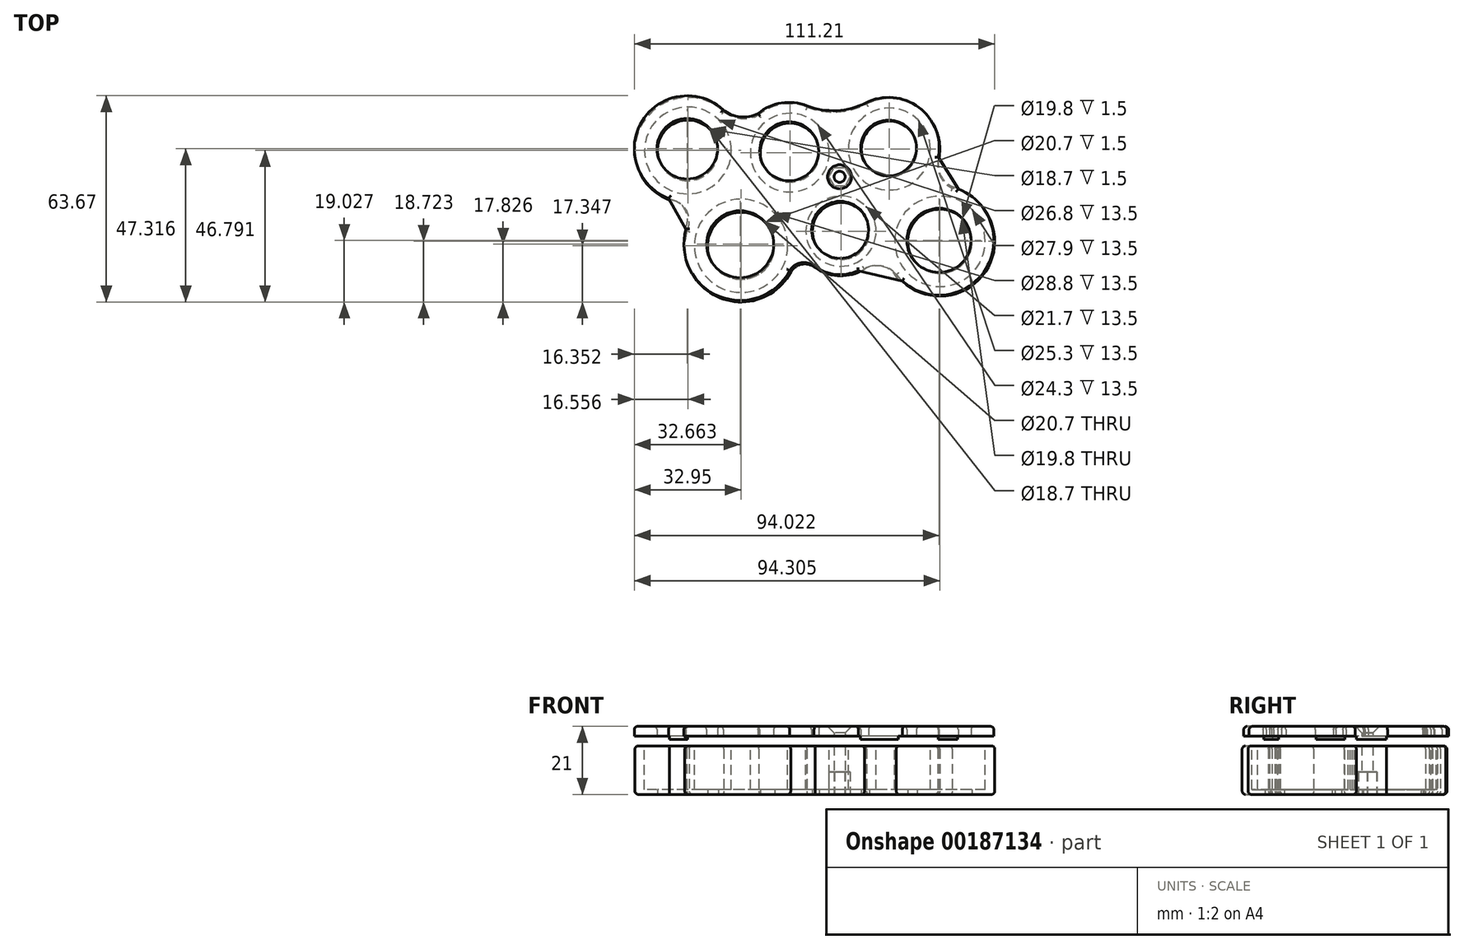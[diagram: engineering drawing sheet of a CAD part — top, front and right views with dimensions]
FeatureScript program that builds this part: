
annotation { "Feature Type Name" : "Feature", "Feature Type Description" : "" }
export const myFeature = defineFeature(function(context is Context, id is Id, definition is map)
    precondition{}
    {
        {
            var Q0;
            Q0=qCreatedBy(makeId("Top.planeOp"),FACE);
            var sketch = newSketch(context, id + "F0", { "sketchPlane" : qUnion([Q0])});
            skArc(sketch, "E0", {"start": v(-18.22, 23.12) * mm, "mid": v(-43.25, 19.71) * mm, "end": v(-35.08, -4.19) * mm});
            skArc(sketch, "E1", {"start": v(7.41, 24.56) * mm, "mid": v(-0.37, 25.32) * mm, "end": v(-7.48, 22.09) * mm});
            skArc(sketch, "E2", {"start": v(48.15, 8.81) * mm, "mid": v(42.1, 24.06) * mm, "end": v(25.77, 25.48) * mm});
            skArc(sketch, "E3", {"start": v(9.86, -25.02) * mm, "mid": v(17.41, -27.58) * mm, "end": v(25.12, -25.54) * mm});
            skArc(sketch, "E4", {"start": v(34.96, -27.17) * mm, "mid": v(62.62, -26.1) * mm, "end": v(52.17, -0.47) * mm});
            skArc(sketch, "E5", {"start": v(-29.65, -13.66) * mm, "mid": v(-19.4, -34.43) * mm, "end": v(2.37, -26.49) * mm});
            skArc(sketch, "E6", {"start": v(-29.65, -13.66) * mm, "mid": v(-29.77, -7.44) * mm, "end": v(-35.08, -4.19) * mm});
            skArc(sketch, "E7", {"start": v(-18.22, 23.12) * mm, "mid": v(-13.01, 20.97) * mm, "end": v(-7.48, 22.09) * mm});
            skArc(sketch, "E8", {"start": v(48.15, 8.81) * mm, "mid": v(48.38, 3.4) * mm, "end": v(52.17, -0.47) * mm});
            skArc(sketch, "E9", {"start": v(34.96, -27.17) * mm, "mid": v(30.34, -24.58) * mm, "end": v(25.12, -25.54) * mm});
            skArc(sketch, "E10", {"start": v(9.86, -25.02) * mm, "mid": v(5.77, -24) * mm, "end": v(2.37, -26.49) * mm});
            skCircle(sketch, "E11", {"center": v(-29.33, 11.12) * mm, "radius": 9.35 * mm});
            skCircle(sketch, "E12", {"center": v(-12.94, -18.32) * mm, "radius": 10.35 * mm});
            skCircle(sketch, "E13", {"center": v(2.1, 10.43) * mm, "radius": 9.1 * mm});
            skCircle(sketch, "E14", {"center": v(17.88, -13.8) * mm, "radius": 8.8 * mm});
            skCircle(sketch, "E15", {"center": v(32.79, 11.55) * mm, "radius": 8.6 * mm});
            skCircle(sketch, "E16", {"center": v(48.42, -16.95) * mm, "radius": 9.9 * mm});
            skPoint(sketch, "E17", {"position": v(17.46, 2.98) * mm});
            skPoint(sketch, "E18.orphan", {"position": v(17.45, 10.99) * mm});
            skPoint(sketch, "E19.orphan", {"position": v(25.33, -1.12) * mm});
            skPoint(sketch, "E20.trimOffspring.end.orphan", {"position": v(10, -1.68) * mm});
            skCircle(sketch, "E21", {"center": v(17.46, 2.98) * mm, "radius": 1.7 * mm});
            skPoint(sketch, "E22.center.orphan", {"position": v(16.6, 25.02) * mm});
            skArc(sketch, "E23", {"start": v(7.41, 24.56) * mm, "mid": v(16.7, 23.01) * mm, "end": v(25.77, 25.48) * mm});
            skSolve(sketch);
        }
        {
            var Q0;
            Q0=makeQuery(id+"F0.imprint","IMPRINT",FACE,{"disambiguationData":[TD([[makeQuery(id+"F0.imprint","IMPRINT",EDGE,{"derivedFrom":sQuery(id+"F0.wireOp",EDGE,"E0")}),1.0]])]});
            extrude(context, id + "F1", {"entities" : qUnion([Q0]), "depth" : 15 * mm});
        }
        {
            var Q0;
            Q0=qCreatedBy(makeId("Top.planeOp"),FACE);
            cPlane(context, id + "F2", {"entities" : qUnion([Q0]), "cplaneType" : CPlaneType.OFFSET, "offset" : 18 * mm, "width" : 150 * mm, "height" : 150 * mm});
        }
        {
            var Q0;
            Q0=makeQuery(id+"F1.opExtrude","CAP_FACE",FACE,{"disambiguationData":[OSD([sQuery(id+"F0.wireOp",EDGE,"E0"),sQuery(id+"F0.wireOp",EDGE,"E1"),sQuery(id+"F0.wireOp",EDGE,"E2"),sQuery(id+"F0.wireOp",EDGE,"E3"),sQuery(id+"F0.wireOp",EDGE,"E4"),sQuery(id+"F0.wireOp",EDGE,"E5"),sQuery(id+"F0.wireOp",EDGE,"E6"),sQuery(id+"F0.wireOp",EDGE,"E7"),sQuery(id+"F0.wireOp",EDGE,"E8"),sQuery(id+"F0.wireOp",EDGE,"E9"),sQuery(id+"F0.wireOp",EDGE,"E10"),sQuery(id+"F0.wireOp",EDGE,"cmuSQvfR-1LlV-bjM8-RssA-lsbDypLqzE8I"),sQuery(id+"F0.wireOp",EDGE,"E22"),sQuery(id+"F0.wireOp",EDGE,"E11"),sQuery(id+"F0.wireOp",EDGE,"E12"),sQuery(id+"F0.wireOp",EDGE,"E13"),sQuery(id+"F0.wireOp",EDGE,"E14"),sQuery(id+"F0.wireOp",EDGE,"E15"),sQuery(id+"F0.wireOp",EDGE,"E16")])],"isStart":false});
            var sketch = newSketch(context, id + "F3", { "sketchPlane" : qUnion([Q0])});
            skCircle(sketch, "E24", {"center": v(-29.33, 11.12) * mm, "radius": 13.4 * mm});
            skCircle(sketch, "E25", {"center": v(-12.94, -18.32) * mm, "radius": 14.4 * mm});
            skCircle(sketch, "E26", {"center": v(17.88, -13.8) * mm, "radius": 10.85 * mm});
            skCircle(sketch, "E27", {"center": v(2.1, 10.43) * mm, "radius": 12.15 * mm});
            skCircle(sketch, "E28", {"center": v(32.79, 11.55) * mm, "radius": 12.65 * mm});
            skCircle(sketch, "E29", {"center": v(48.42, -16.95) * mm, "radius": 13.95 * mm});
            skSolve(sketch);
        }
        {
            var Q0;
            Q0=makeQuery(id+"F3.imprint","IMPRINT",FACE,{"disambiguationData":[TD([[makeQuery(id+"F3.imprint","IMPRINT",EDGE,{"derivedFrom":sQuery(id+"F3.wireOp",EDGE,"E24")}),1.0]])]});
            var Q1;
            Q1=makeQuery(id+"F3.imprint","IMPRINT",FACE,{"disambiguationData":[TD([[makeQuery(id+"F3.imprint","IMPRINT",EDGE,{"derivedFrom":sQuery(id+"F3.wireOp",EDGE,"E27")}),1.0]])]});
            var Q2;
            Q2=makeQuery(id+"F3.imprint","IMPRINT",FACE,{"disambiguationData":[TD([[makeQuery(id+"F3.imprint","IMPRINT",EDGE,{"derivedFrom":sQuery(id+"F3.wireOp",EDGE,"E28")}),1.0]])]});
            var Q3;
            Q3=makeQuery(id+"F3.imprint","IMPRINT",FACE,{"disambiguationData":[TD([[makeQuery(id+"F3.imprint","IMPRINT",EDGE,{"derivedFrom":sQuery(id+"F3.wireOp",EDGE,"E26")}),1.0]])]});
            var Q4;
            Q4=makeQuery(id+"F3.imprint","IMPRINT",FACE,{"disambiguationData":[TD([[makeQuery(id+"F3.imprint","IMPRINT",EDGE,{"derivedFrom":sQuery(id+"F3.wireOp",EDGE,"E25")}),1.0]])]});
            var Q5;
            Q5=makeQuery(id+"F3.imprint","IMPRINT",FACE,{"disambiguationData":[TD([[makeQuery(id+"F3.imprint","IMPRINT",EDGE,{"derivedFrom":sQuery(id+"F3.wireOp",EDGE,"E29")}),1.0]])]});
            extrude(context, id + "F4", {"entities" : qUnion([Q0, Q1, Q2, Q3, Q4, Q5]), "operationType" : NewBodyOperationType.REMOVE, "oppositeDirection" : true, "depth" : 13.5 * mm});
        }
        {
            var Q0;
            Q0=qCreatedBy(makeId("Top.planeOp"),FACE);
            var sketch = newSketch(context, id + "F5", { "sketchPlane" : qUnion([Q0])});
            skPoint(sketch, "E30", {"position": v(17.46, 2.98) * mm});
            skCircle(sketch, "E31.cCircle", {"center": v(17.46, 2.98) * mm, "radius": 2.86 * mm, "construction": true});
            skLineSegment(sketch, "E31.0", {"start": v(19.06, 5.87) * mm, "end": v(20.76, 3.03) * mm});
            skLineSegment(sketch, "E31.1", {"start": v(20.76, 3.03) * mm, "end": v(19.15, 0.15) * mm});
            skLineSegment(sketch, "E31.2", {"start": v(19.15, 0.15) * mm, "end": v(15.85, 0.1) * mm});
            skLineSegment(sketch, "E31.3", {"start": v(15.85, 0.1) * mm, "end": v(14.16, 2.93) * mm});
            skLineSegment(sketch, "E31.4", {"start": v(14.16, 2.93) * mm, "end": v(15.76, 5.81) * mm});
            skLineSegment(sketch, "E31.5", {"start": v(15.76, 5.81) * mm, "end": v(19.06, 5.87) * mm});
            skPoint(sketch, "E31.0.midPoint", {"position": v(19.9, 4.45) * mm});
            skSolve(sketch);
        }
        {
            var Q0;
            Q0=makeQuery(id+"F5.imprint","IMPRINT",FACE,{"disambiguationData":[TD([[makeQuery(id+"F5.imprint","IMPRINT",EDGE,{"derivedFrom":sQuery(id+"F5.wireOp",EDGE,"E31.0")}),-1.0]])]});
            extrude(context, id + "F6", {"entities" : qUnion([Q0]), "operationType" : NewBodyOperationType.REMOVE, "depth" : 7 * mm});
        }
        {
            var Q0;
            Q0=qCreatedBy(id+"F2.planeOp",FACE);
            var sketch = newSketch(context, id + "F7", { "sketchPlane" : qUnion([Q0])});
            skArc(sketch, "E32", {"start": v(-18.43, 23.64) * mm, "mid": v(-43.45, 20.24) * mm, "end": v(-35.28, -3.66) * mm});
            skArc(sketch, "E33", {"start": v(7.4, 24.92) * mm, "mid": v(-0.47, 25.78) * mm, "end": v(-7.7, 22.52) * mm});
            skArc(sketch, "E34", {"start": v(47.94, 9.16) * mm, "mid": v(41.9, 24.4) * mm, "end": v(25.57, 25.83) * mm});
            skArc(sketch, "E35", {"start": v(9.59, -24.63) * mm, "mid": v(17.14, -27.2) * mm, "end": v(24.85, -25.15) * mm});
            skArc(sketch, "E36", {"start": v(34.68, -26.87) * mm, "mid": v(62.34, -25.8) * mm, "end": v(51.88, -0.16) * mm});
            skArc(sketch, "E37", {"start": v(-29.94, -13.18) * mm, "mid": v(-19.68, -33.95) * mm, "end": v(2.08, -26) * mm});
            skArc(sketch, "E38", {"start": v(-29.94, -13.18) * mm, "mid": v(-30, -6.96) * mm, "end": v(-35.28, -3.66) * mm});
            skArc(sketch, "E39", {"start": v(-18.43, 23.64) * mm, "mid": v(-13.23, 21.45) * mm, "end": v(-7.7, 22.52) * mm});
            skArc(sketch, "E40", {"start": v(47.94, 9.16) * mm, "mid": v(48.13, 3.75) * mm, "end": v(51.88, -0.16) * mm});
            skArc(sketch, "E41", {"start": v(34.68, -26.87) * mm, "mid": v(30.07, -24.23) * mm, "end": v(24.85, -25.15) * mm});
            skArc(sketch, "E42", {"start": v(9.59, -24.63) * mm, "mid": v(5.51, -23.57) * mm, "end": v(2.08, -26) * mm});
            skCircle(sketch, "E43", {"center": v(-29.54, 11.65) * mm, "radius": 9.35 * mm});
            skCircle(sketch, "E44", {"center": v(-13.23, -17.84) * mm, "radius": 10.35 * mm});
            skCircle(sketch, "E45", {"center": v(1.9, 10.86) * mm, "radius": 9.1 * mm});
            skCircle(sketch, "E46", {"center": v(17.6, -13.4) * mm, "radius": 8.8 * mm});
            skCircle(sketch, "E47", {"center": v(32.59, 11.9) * mm, "radius": 8.6 * mm});
            skCircle(sketch, "E48", {"center": v(48.13, -16.64) * mm, "radius": 9.9 * mm});
            skLineSegment(sketch, "E49", {"start": v(-29.94, -13.18) * mm, "end": v(-35.28, -3.66) * mm});
            skArc(sketch, "E50", {"start": v(-30.11, -12.87) * mm, "mid": v(-30.27, -7.1) * mm, "end": v(-35.1, -3.97) * mm});
            skArc(sketch, "E51", {"start": v(34.2, -26.79) * mm, "mid": v(30.02, -24.52) * mm, "end": v(25.32, -25.23) * mm});
            skLineSegment(sketch, "E52", {"start": v(54.05, -0.81) * mm, "end": v(47.94, 9.16) * mm});
            skArc(sketch, "E53", {"start": v(48.15, 8.83) * mm, "mid": v(48.9, 2.9) * mm, "end": v(53.84, -0.48) * mm});
            skArc(sketch, "E54", {"start": v(35.61, -28.94) * mm, "mid": v(30.44, -24.61) * mm, "end": v(23.89, -26.18) * mm});
            skLineSegment(sketch, "E55", {"start": v(23.2, -26.02) * mm, "end": v(36.86, -29.23) * mm});
            skCircle(sketch, "E56", {"center": v(17.46, 2.98) * mm, "radius": 1.7 * mm});
            skPoint(sketch, "E57.center.orphan", {"position": v(16.49, 25.38) * mm});
            skArc(sketch, "E58", {"start": v(7.4, 24.92) * mm, "mid": v(16.59, 23.41) * mm, "end": v(25.57, 25.83) * mm});
            skSolve(sketch);
        }
        {
            var Q0;
            Q0 = qSketchRegion(id + "F7", true);
            extrude(context, id + "F8", {"entities" : qUnion([Q0]), "depth" : 3 * mm});
        }
        {
            var Q0;
            {var subQ0=sQuery(id+"F7.wireOp",EDGE,"abFJn2rG-QnjB-3oZD-kfx5-oWbmogYZg01U");Q0=makeQuery(id+"F7.imprint","IMPRINT",FACE,{"disambiguationData":[TD([[makeQuery(id+"F7.imprint","IMPRINT",EDGE,{"derivedFrom":subQ0}),1.0]])]});}
            var Q1;
            {var subQ0=sQuery(id+"F7.wireOp",EDGE,"E50");Q1=makeQuery(id+"F7.imprint","IMPRINT",FACE,{"disambiguationData":[TD([[makeQuery(id+"F7.imprint","IMPRINT",EDGE,{"derivedFrom":subQ0}),1.0]])]});}
            var Q2;
            {var subQ0=sQuery(id+"F7.wireOp",EDGE,"E51");Q2=makeQuery(id+"F7.imprint","IMPRINT",FACE,{"disambiguationData":[TD([[makeQuery(id+"F7.imprint","IMPRINT",EDGE,{"derivedFrom":subQ0}),1.0]])]});}
            var Q3;
            {var subQ0=sQuery(id+"F7.wireOp",EDGE,"E53");Q3=makeQuery(id+"F7.imprint","IMPRINT",FACE,{"disambiguationData":[TD([[makeQuery(id+"F7.imprint","IMPRINT",EDGE,{"derivedFrom":subQ0}),1.0]])]});}
            var Q4;
            {var subQ1=sQuery(id+"F7.wireOp",EDGE,"E54");var subQ3=makeQuery(id+"F7.imprint","IMPRINT",VERTEX,{"disambiguationData":[OD(0.0)],"derivedFrom":subQ1});Q4=makeQuery(id+"F7.imprint","IMPRINT",FACE,{"disambiguationData":[TD([[makeQuery(id+"F7.imprint","IMPRINT",EDGE,{"disambiguationData":[TD([[subQ3,-1.0]])],"derivedFrom":subQ1}),1.0]])]});}
            extrude(context, id + "F9", {"entities" : qUnion([Q0, Q1, Q2, Q3, Q4]), "operationType" : NewBodyOperationType.ADD, "oppositeDirection" : true, "depth" : 1 * mm});
        }
        {
            var Q0;
            Q0=makeQuery(id+"F1.opExtrude","CAP_EDGE",EDGE,{"disambiguationData":[OSD([sQuery(id+"F0.wireOp",EDGE,"E2")])],"isStart":true});
            var Q1;
            Q1=makeQuery(id+"F1.opExtrude","CAP_EDGE",EDGE,{"disambiguationData":[OSD([sQuery(id+"F0.wireOp",EDGE,"cmuSQvfR-1LlV-bjM8-RssA-lsbDypLqzE8I")])],"isStart":true});
            var Q2;
            Q2=makeQuery(id+"F1.opExtrude","CAP_EDGE",EDGE,{"disambiguationData":[OSD([sQuery(id+"F0.wireOp",EDGE,"E1")])],"isStart":true});
            var Q3;
            Q3=makeQuery(id+"F1.opExtrude","CAP_EDGE",EDGE,{"disambiguationData":[OSD([sQuery(id+"F0.wireOp",EDGE,"E7")])],"isStart":true});
            var Q4;
            Q4=makeQuery(id+"F1.opExtrude","CAP_EDGE",EDGE,{"disambiguationData":[OSD([sQuery(id+"F0.wireOp",EDGE,"E0")])],"isStart":true});
            var Q5;
            Q5=makeQuery(id+"F1.opExtrude","CAP_EDGE",EDGE,{"disambiguationData":[OSD([sQuery(id+"F0.wireOp",EDGE,"E6")])],"isStart":true});
            var Q6;
            Q6=makeQuery(id+"F1.opExtrude","CAP_EDGE",EDGE,{"disambiguationData":[OSD([sQuery(id+"F0.wireOp",EDGE,"E5")])],"isStart":true});
            var Q7;
            Q7=makeQuery(id+"F1.opExtrude","CAP_EDGE",EDGE,{"disambiguationData":[OSD([sQuery(id+"F0.wireOp",EDGE,"E10")])],"isStart":true});
            var Q8;
            Q8=makeQuery(id+"F1.opExtrude","CAP_EDGE",EDGE,{"disambiguationData":[OSD([sQuery(id+"F0.wireOp",EDGE,"E3")])],"isStart":true});
            var Q9;
            Q9=makeQuery(id+"F1.opExtrude","CAP_EDGE",EDGE,{"disambiguationData":[OSD([sQuery(id+"F0.wireOp",EDGE,"E9")])],"isStart":true});
            var Q10;
            Q10=makeQuery(id+"F1.opExtrude","CAP_EDGE",EDGE,{"disambiguationData":[OSD([sQuery(id+"F0.wireOp",EDGE,"E4")])],"isStart":true});
            var Q11;
            Q11=makeQuery(id+"F1.opExtrude","CAP_EDGE",EDGE,{"disambiguationData":[OSD([sQuery(id+"F0.wireOp",EDGE,"E8")])],"isStart":true});
            var Q12;
            Q12=makeQuery(id+"F1.opExtrude","CAP_EDGE",EDGE,{"disambiguationData":[OSD([sQuery(id+"F0.wireOp",EDGE,"E2")])],"isStart":false});
            var Q13;
            Q13=makeQuery(id+"F1.opExtrude","CAP_EDGE",EDGE,{"disambiguationData":[OSD([sQuery(id+"F0.wireOp",EDGE,"cmuSQvfR-1LlV-bjM8-RssA-lsbDypLqzE8I")])],"isStart":false});
            var Q14;
            Q14=makeQuery(id+"F1.opExtrude","CAP_EDGE",EDGE,{"disambiguationData":[OSD([sQuery(id+"F0.wireOp",EDGE,"E1")])],"isStart":false});
            var Q15;
            Q15=makeQuery(id+"F1.opExtrude","CAP_EDGE",EDGE,{"disambiguationData":[OSD([sQuery(id+"F0.wireOp",EDGE,"E7")])],"isStart":false});
            var Q16;
            Q16=makeQuery(id+"F1.opExtrude","CAP_EDGE",EDGE,{"disambiguationData":[OSD([sQuery(id+"F0.wireOp",EDGE,"E0")])],"isStart":false});
            var Q17;
            Q17=makeQuery(id+"F1.opExtrude","CAP_EDGE",EDGE,{"disambiguationData":[OSD([sQuery(id+"F0.wireOp",EDGE,"E6")])],"isStart":false});
            var Q18;
            Q18=makeQuery(id+"F1.opExtrude","CAP_EDGE",EDGE,{"disambiguationData":[OSD([sQuery(id+"F0.wireOp",EDGE,"E5")])],"isStart":false});
            var Q19;
            Q19=makeQuery(id+"F1.opExtrude","CAP_EDGE",EDGE,{"disambiguationData":[OSD([sQuery(id+"F0.wireOp",EDGE,"E10")])],"isStart":false});
            var Q20;
            Q20=makeQuery(id+"F1.opExtrude","CAP_EDGE",EDGE,{"disambiguationData":[OSD([sQuery(id+"F0.wireOp",EDGE,"E3")])],"isStart":false});
            var Q21;
            Q21=makeQuery(id+"F1.opExtrude","CAP_EDGE",EDGE,{"disambiguationData":[OSD([sQuery(id+"F0.wireOp",EDGE,"E9")])],"isStart":false});
            var Q22;
            Q22=makeQuery(id+"F1.opExtrude","CAP_EDGE",EDGE,{"disambiguationData":[OSD([sQuery(id+"F0.wireOp",EDGE,"E4")])],"isStart":false});
            var Q23;
            Q23=makeQuery(id+"F1.opExtrude","CAP_EDGE",EDGE,{"disambiguationData":[OSD([sQuery(id+"F0.wireOp",EDGE,"E8")])],"isStart":false});
            var Q24;
            Q24=makeQuery(id+"F1.opExtrude","CAP_EDGE",EDGE,{"disambiguationData":[OSD([sQuery(id+"F0.wireOp",EDGE,"E23")])],"isStart":true});
            var Q25;
            Q25=makeQuery(id+"F1.opExtrude","CAP_EDGE",EDGE,{"disambiguationData":[OSD([sQuery(id+"F0.wireOp",EDGE,"E23")])],"isStart":false});
            fillet(context, id + "F10", {"entities" : qUnion([Q0, Q1, Q2, Q3, Q4, Q5, Q6, Q7, Q8, Q9, Q10, Q11, Q12, Q13, Q14, Q15, Q16, Q17, Q18, Q19, Q20, Q21, Q22, Q23, Q24, Q25]), "radius" : 1 * mm, "tangentPropagation" : true, "allowEdgeOverflow" : false});
        }
        {
            var Q0;
            Q0=makeQuery(id+"F8.opExtrude","CAP_EDGE",EDGE,{"disambiguationData":[OSD([sQuery(id+"F7.wireOp",EDGE,"E45")])],"isStart":false});
            var Q1;
            Q1=makeQuery(id+"F8.opExtrude","CAP_EDGE",EDGE,{"disambiguationData":[OSD([sQuery(id+"F7.wireOp",EDGE,"E43")])],"isStart":false});
            var Q2;
            Q2=makeQuery(id+"F8.opExtrude","CAP_EDGE",EDGE,{"disambiguationData":[OSD([sQuery(id+"F7.wireOp",EDGE,"E44")])],"isStart":false});
            var Q3;
            Q3=makeQuery(id+"F8.opExtrude","CAP_EDGE",EDGE,{"disambiguationData":[OSD([sQuery(id+"F7.wireOp",EDGE,"E46")])],"isStart":false});
            var Q4;
            Q4=makeQuery(id+"F8.opExtrude","CAP_EDGE",EDGE,{"disambiguationData":[OSD([sQuery(id+"F7.wireOp",EDGE,"E47")])],"isStart":false});
            var Q5;
            Q5=makeQuery(id+"F8.opExtrude","CAP_EDGE",EDGE,{"disambiguationData":[OSD([sQuery(id+"F7.wireOp",EDGE,"E48")])],"isStart":false});
            var Q6;
            Q6=makeQuery(id+"F8.opExtrude","CAP_EDGE",EDGE,{"disambiguationData":[OSD([sQuery(id+"F7.wireOp",EDGE,"E52")])],"isStart":false});
            var Q7;
            Q7=makeQuery(id+"F8.opExtrude","CAP_EDGE",EDGE,{"disambiguationData":[OSD([sQuery(id+"F7.wireOp",EDGE,"E36")])],"isStart":false});
            var Q8;
            Q8=makeQuery(id+"F8.opExtrude","CAP_EDGE",EDGE,{"disambiguationData":[OSD([sQuery(id+"F7.wireOp",EDGE,"E55")])],"isStart":false});
            var Q9;
            Q9=makeQuery(id+"F8.opExtrude","CAP_EDGE",EDGE,{"disambiguationData":[OSD([sQuery(id+"F7.wireOp",EDGE,"E35")])],"isStart":false});
            var Q10;
            Q10=makeQuery(id+"F8.opExtrude","CAP_EDGE",EDGE,{"disambiguationData":[OSD([sQuery(id+"F7.wireOp",EDGE,"E42")])],"isStart":false});
            var Q11;
            Q11=makeQuery(id+"F8.opExtrude","CAP_EDGE",EDGE,{"disambiguationData":[OSD([sQuery(id+"F7.wireOp",EDGE,"E37")])],"isStart":false});
            var Q12;
            Q12=makeQuery(id+"F8.opExtrude","CAP_EDGE",EDGE,{"disambiguationData":[OSD([sQuery(id+"F7.wireOp",EDGE,"E49")])],"isStart":false});
            var Q13;
            Q13=makeQuery(id+"F8.opExtrude","CAP_EDGE",EDGE,{"disambiguationData":[OSD([sQuery(id+"F7.wireOp",EDGE,"E32")])],"isStart":false});
            var Q14;
            Q14=makeQuery(id+"F8.opExtrude","CAP_EDGE",EDGE,{"disambiguationData":[OSD([sQuery(id+"F7.wireOp",EDGE,"E39")])],"isStart":false});
            var Q15;
            Q15=makeQuery(id+"F8.opExtrude","CAP_EDGE",EDGE,{"disambiguationData":[OSD([sQuery(id+"F7.wireOp",EDGE,"E33")])],"isStart":false});
            var Q16;
            Q16=makeQuery(id+"F8.opExtrude","CAP_EDGE",EDGE,{"disambiguationData":[OSD([sQuery(id+"F7.wireOp",EDGE,"69c1c0b9-9592-4324-a081-7276ba0f928f")])],"isStart":false});
            var Q17;
            Q17=makeQuery(id+"F8.opExtrude","CAP_EDGE",EDGE,{"disambiguationData":[OSD([sQuery(id+"F7.wireOp",EDGE,"E34")])],"isStart":false});
            var Q18;
            Q18=makeQuery(id+"F8.opExtrude","CAP_EDGE",EDGE,{"disambiguationData":[OSD([sQuery(id+"F7.wireOp",EDGE,"E58")])],"isStart":false});
            fillet(context, id + "F11", {"entities" : qUnion([Q0, Q1, Q2, Q3, Q4, Q5, Q6, Q7, Q8, Q9, Q10, Q11, Q12, Q13, Q14, Q15, Q16, Q17, Q18]), "radius" : 1 * mm, "tangentPropagation" : true, "allowEdgeOverflow" : false});
        }
        {
            var Q0;
            Q0=makeQuery(id+"F8.opExtrude","CAP_EDGE",EDGE,{"disambiguationData":[OSD([sQuery(id+"F7.wireOp",EDGE,"E56")])],"isStart":false});
            chamfer(context, id + "F12", {"entities" : qUnion([Q0]), "width" : 2 * mm, "tangentPropagation" : true});
        }
    });
